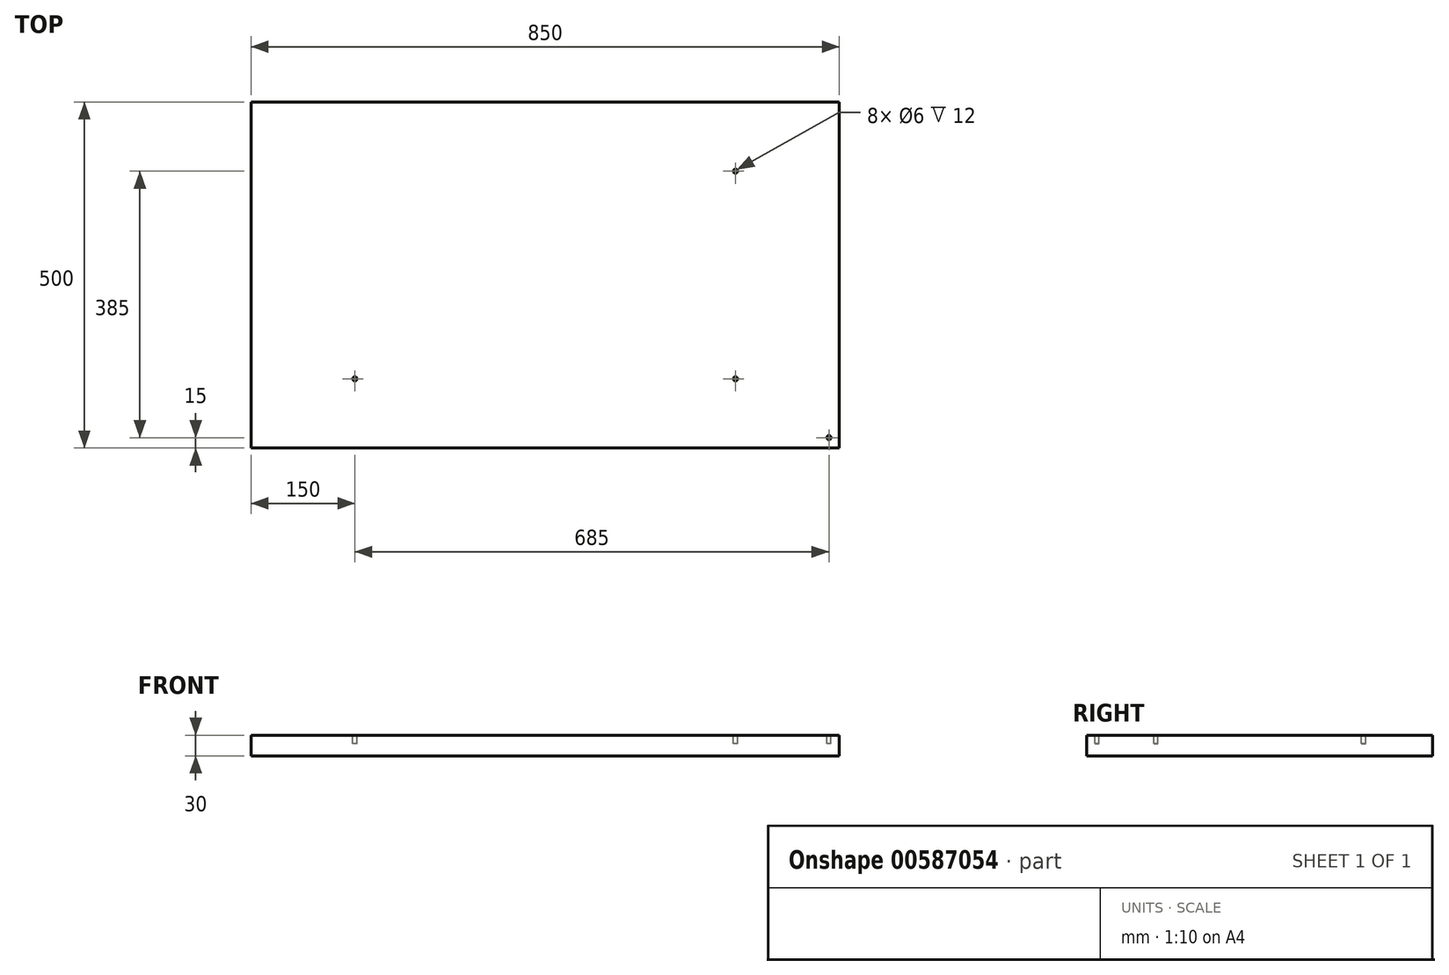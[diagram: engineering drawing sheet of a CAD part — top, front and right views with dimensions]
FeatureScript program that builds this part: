
annotation { "Feature Type Name" : "Feature", "Feature Type Description" : "" }
export const myFeature = defineFeature(function(context is Context, id is Id, definition is map)
    precondition{}
    {
        {
            var Q0;
            Q0=qCreatedBy(makeId("Top.planeOp"),FACE);
            var sketch = newSketch(context, id + "F0", { "sketchPlane" : qUnion([Q0])});
            skLineSegment(sketch, "E0.bottom", {"start": v(0, 0) * mm, "end": v(-850, 0) * mm});
            skLineSegment(sketch, "E0.top", {"start": v(0, 500) * mm, "end": v(-850, 500) * mm});
            skLineSegment(sketch, "E0.left", {"start": v(0, 0) * mm, "end": v(0, 500) * mm});
            skLineSegment(sketch, "E0.right", {"start": v(-850, 0) * mm, "end": v(-850, 500) * mm});
            skSolve(sketch);
        }
        {
            var Q0;
            Q0 = qSketchRegion(id + "F0", true);
            extrude(context, id + "F1", {"entities" : qUnion([Q0]), "depth" : 30 * mm, "offsetDistance" : 25 * mm});
        }
        {
            var Q0;
            Q0=makeQuery(id+"F1.opExtrude","CAP_FACE",FACE,{"disambiguationData":[OSD([sQuery(id+"F0.wireOp",EDGE,"E0.bottom"),sQuery(id+"F0.wireOp",EDGE,"E0.top"),sQuery(id+"F0.wireOp",EDGE,"E0.left"),sQuery(id+"F0.wireOp",EDGE,"E0.right")])],"isStart":false});
            var sketch = newSketch(context, id + "F2", { "sketchPlane" : qUnion([Q0])});
            skCircle(sketch, "E1", {"center": v(-150, 100) * mm, "radius": 3 * mm});
            skSolve(sketch);
        }
        {
            var Q0;
            Q0=makeQuery(id+"F2.imprint","IMPRINT",FACE,{"disambiguationData":[TD([[makeQuery(id+"F2.imprint","IMPRINT",EDGE,{"derivedFrom":sQuery(id+"F2.wireOp",EDGE,"E1")}),1.0]])]});
            extrude(context, id + "F3", {"entities" : qUnion([Q0]), "operationType" : NewBodyOperationType.REMOVE, "oppositeDirection" : true, "depth" : 12 * mm, "offsetDistance" : 25 * mm});
        }
        {
            var Q0;
            Q0=makeQuery(id+"F1.opExtrude","CAP_FACE",FACE,{"disambiguationData":[OSD([sQuery(id+"F0.wireOp",EDGE,"E0.bottom"),sQuery(id+"F0.wireOp",EDGE,"E0.top"),sQuery(id+"F0.wireOp",EDGE,"E0.left"),sQuery(id+"F0.wireOp",EDGE,"E0.right")])],"isStart":false});
            var sketch = newSketch(context, id + "F4", { "sketchPlane" : qUnion([Q0])});
            skCircle(sketch, "E2", {"center": v(-150, 400) * mm, "radius": 3 * mm});
            skSolve(sketch);
        }
        {
            var Q0;
            Q0=makeQuery(id+"F4.imprint","IMPRINT",FACE,{"disambiguationData":[TD([[makeQuery(id+"F4.imprint","IMPRINT",EDGE,{"derivedFrom":sQuery(id+"F4.wireOp",EDGE,"E2")}),1.0]])]});
            extrude(context, id + "F5", {"entities" : qUnion([Q0]), "operationType" : NewBodyOperationType.REMOVE, "oppositeDirection" : true, "depth" : 12 * mm, "offsetDistance" : 25 * mm});
        }
        {
            var Q0;
            Q0=makeQuery(id+"F1.opExtrude","CAP_FACE",FACE,{"disambiguationData":[OSD([sQuery(id+"F0.wireOp",EDGE,"E0.bottom"),sQuery(id+"F0.wireOp",EDGE,"E0.top"),sQuery(id+"F0.wireOp",EDGE,"E0.left"),sQuery(id+"F0.wireOp",EDGE,"E0.right")])],"isStart":false});
            var sketch = newSketch(context, id + "F6", { "sketchPlane" : qUnion([Q0])});
            skCircle(sketch, "E3", {"center": v(-700, 100) * mm, "radius": 3 * mm});
            skSolve(sketch);
        }
        {
            var Q0;
            Q0=makeQuery(id+"F6.imprint","IMPRINT",FACE,{"disambiguationData":[TD([[makeQuery(id+"F6.imprint","IMPRINT",EDGE,{"derivedFrom":sQuery(id+"F6.wireOp",EDGE,"E3")}),1.0]])]});
            extrude(context, id + "F7", {"entities" : qUnion([Q0]), "operationType" : NewBodyOperationType.REMOVE, "oppositeDirection" : true, "depth" : 12 * mm, "offsetDistance" : 25 * mm});
        }
        {
            var Q0;
            Q0=makeQuery(id+"F1.opExtrude","CAP_FACE",FACE,{"disambiguationData":[OSD([sQuery(id+"F0.wireOp",EDGE,"E0.bottom"),sQuery(id+"F0.wireOp",EDGE,"E0.top"),sQuery(id+"F0.wireOp",EDGE,"E0.left"),sQuery(id+"F0.wireOp",EDGE,"E0.right")])],"isStart":false});
            var sketch = newSketch(context, id + "F8", { "sketchPlane" : qUnion([Q0])});
            skCircle(sketch, "E4", {"center": v(-15, 15) * mm, "radius": 3 * mm});
            skSolve(sketch);
        }
        {
            var Q0;
            Q0=makeQuery(id+"F8.imprint","IMPRINT",FACE,{"disambiguationData":[TD([[makeQuery(id+"F8.imprint","IMPRINT",EDGE,{"derivedFrom":sQuery(id+"F8.wireOp",EDGE,"E4")}),1.0]])]});
            extrude(context, id + "F9", {"entities" : qUnion([Q0]), "operationType" : NewBodyOperationType.REMOVE, "oppositeDirection" : true, "depth" : 12 * mm, "offsetDistance" : 25 * mm});
        }
    });
